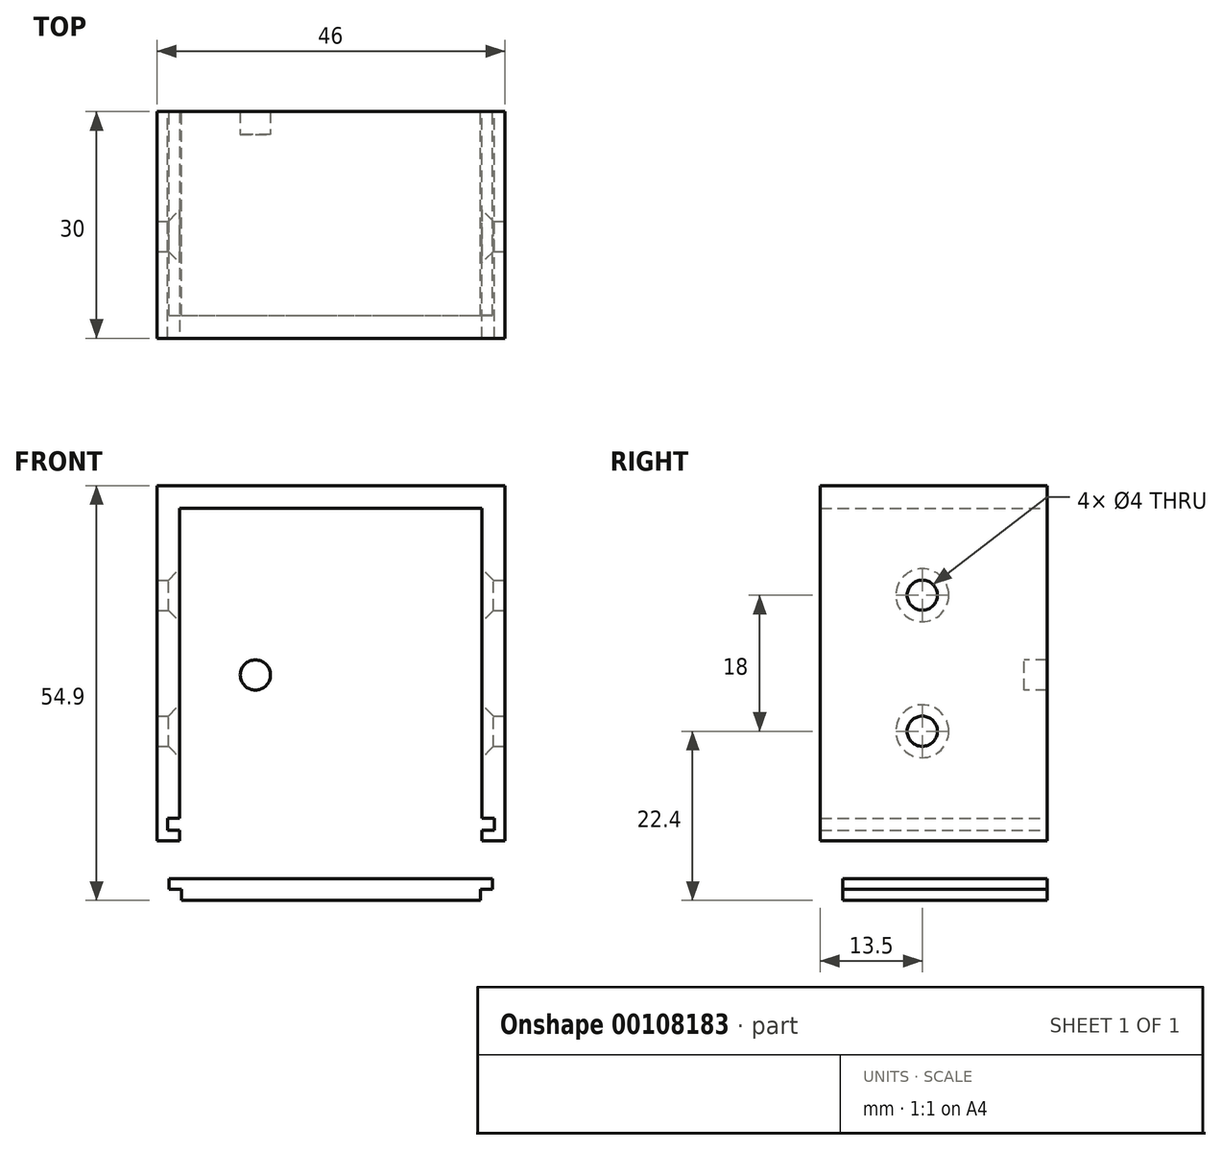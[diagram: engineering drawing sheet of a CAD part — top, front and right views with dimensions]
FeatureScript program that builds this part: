
annotation { "Feature Type Name" : "Feature", "Feature Type Description" : "" }
export const myFeature = defineFeature(function(context is Context, id is Id, definition is map)
    precondition{}
    {
        {
            var Q0;
            Q0=qCreatedBy(makeId("Front.planeOp"),FACE);
            var sketch = newSketch(context, id + "F0", { "sketchPlane" : qUnion([Q0])});
            skLineSegment(sketch, "E0", {"start": v(0, 44) * mm, "end": v(20, 44) * mm});
            skLineSegment(sketch, "E1", {"start": v(20, 44) * mm, "end": v(20, 3) * mm});
            skLineSegment(sketch, "E2", {"start": v(20, 3) * mm, "end": v(21.6, 3) * mm});
            skLineSegment(sketch, "E3", {"start": v(21.6, 3) * mm, "end": v(21.6, 1.4) * mm});
            skLineSegment(sketch, "E4", {"start": v(21.6, 1.4) * mm, "end": v(20, 1.4) * mm});
            skLineSegment(sketch, "E5", {"start": v(20, 1.4) * mm, "end": v(20, 0) * mm});
            skLineSegment(sketch, "E6", {"start": v(20, 0) * mm, "end": v(23, 0) * mm});
            skLineSegment(sketch, "E7", {"start": v(23, 0) * mm, "end": v(23, 47) * mm});
            skLineSegment(sketch, "E8", {"start": v(23, 47) * mm, "end": v(0, 47) * mm});
            skLineSegment(sketch, "E9.MirrorCS", {"start": v(-23, 47) * mm, "end": v(0, 47) * mm});
            skLineSegment(sketch, "E10.MirrorCS", {"start": v(-23, 0) * mm, "end": v(-23, 47) * mm});
            skLineSegment(sketch, "E11.MirrorCS", {"start": v(0, 44) * mm, "end": v(-20, 44) * mm});
            skLineSegment(sketch, "E12.MirrorCS", {"start": v(-20, 44) * mm, "end": v(-20, 3) * mm});
            skLineSegment(sketch, "E13.MirrorCS", {"start": v(-20, 3) * mm, "end": v(-21.6, 3) * mm});
            skLineSegment(sketch, "E14.MirrorCS", {"start": v(-21.6, 3) * mm, "end": v(-21.6, 1.4) * mm});
            skLineSegment(sketch, "E15.MirrorCS", {"start": v(-21.6, 1.4) * mm, "end": v(-20, 1.4) * mm});
            skLineSegment(sketch, "E16.MirrorCS", {"start": v(-20, 1.4) * mm, "end": v(-20, 0) * mm});
            skLineSegment(sketch, "E17.MirrorCS", {"start": v(-20, 0) * mm, "end": v(-23, 0) * mm});
            skSolve(sketch);
        }
        {
            var Q0;
            Q0=makeQuery(id+"F0.imprint","IMPRINT",FACE,{"disambiguationData":[TD([[makeQuery(id+"F0.imprint","IMPRINT",EDGE,{"derivedFrom":sQuery(id+"F0.wireOp",EDGE,"E0")}),1.0]])]});
            extrude(context, id + "F1", {"entities" : qUnion([Q0]), "depth" : 30 * mm});
        }
        {
            var Q0;
            Q0=qCreatedBy(makeId("Top.planeOp"),FACE);
            var sketch = newSketch(context, id + "F2", { "sketchPlane" : qUnion([Q0])});
            skLineSegment(sketch, "E18", {"start": v(-23, 0) * mm, "end": v(-23, -3) * mm});
            skLineSegment(sketch, "E19", {"start": v(-23, -3) * mm, "end": v(23, -3) * mm});
            skLineSegment(sketch, "E20", {"start": v(23, -3) * mm, "end": v(23, 0) * mm});
            skLineSegment(sketch, "E21", {"start": v(23, 0) * mm, "end": v(-23, 0) * mm});
            skSolve(sketch);
        }
        {
            var Q0;
            Q0=makeQuery(id+"F2.imprint","IMPRINT",FACE,{"disambiguationData":[TD([[makeQuery(id+"F2.imprint","IMPRINT",EDGE,{"derivedFrom":sQuery(id+"F2.wireOp",EDGE,"E18")}),1.0]])]});
            extrude(context, id + "F3", {"entities" : qUnion([Q0]), "operationType" : NewBodyOperationType.ADD, "depth" : 47 * mm});
        }
        {
            var Q0;
            Q0=makeQuery(id+"F3.opExtrude","SWEPT_FACE",FACE,{"disambiguationData":[OSD([sQuery(id+"F2.wireOp",EDGE,"E19")])]});
            var sketch = newSketch(context, id + "F4", { "sketchPlane" : qUnion([Q0])});
            skCircle(sketch, "E22", {"center": v(10, 21.94) * mm, "radius": 2 * mm});
            skCircle(sketch, "E23.MirrorC", {"center": v(-10, 21.94) * mm, "radius": 2 * mm});
            skSolve(sketch);
        }
        {
            var Q0;
            Q0=makeQuery(id+"F4.imprint","IMPRINT",FACE,{"disambiguationData":[TD([[makeQuery(id+"F4.imprint","IMPRINT",EDGE,{"derivedFrom":sQuery(id+"F4.wireOp",EDGE,"E23.MirrorC")}),-1.0]])]});
            var Q1;
            Q1=makeQuery(id+"F4.imprint","IMPRINT",FACE,{"disambiguationData":[TD([[makeQuery(id+"F4.imprint","IMPRINT",EDGE,{"derivedFrom":sQuery(id+"F4.wireOp",EDGE,"E22")}),1.0]])]});
            extrude(context, id + "F5", {"entities" : qUnion([Q0, Q1]), "operationType" : NewBodyOperationType.REMOVE, "endBound" : BoundingType.THROUGH_ALL, "oppositeDirection" : true, "depth" : 25 * mm});
        }
        {
            var Q0;
            Q0=qCreatedBy(makeId("Front.planeOp"),FACE);
            var sketch = newSketch(context, id + "F6", { "sketchPlane" : qUnion([Q0])});
            skLineSegment(sketch, "E24", {"start": v(0, -5) * mm, "end": v(21.4, -5) * mm});
            skLineSegment(sketch, "E25", {"start": v(21.4, -5) * mm, "end": v(21.4, -6.4) * mm});
            skLineSegment(sketch, "E26", {"start": v(21.4, -6.4) * mm, "end": v(19.8, -6.4) * mm});
            skLineSegment(sketch, "E27", {"start": v(19.8, -6.4) * mm, "end": v(19.8, -7.9) * mm});
            skLineSegment(sketch, "E28", {"start": v(19.8, -7.9) * mm, "end": v(0, -7.9) * mm});
            skLineSegment(sketch, "E29.MirrorCS", {"start": v(0, -5) * mm, "end": v(-21.4, -5) * mm});
            skLineSegment(sketch, "E30.MirrorCS", {"start": v(-19.8, -7.9) * mm, "end": v(0, -7.9) * mm});
            skLineSegment(sketch, "E31.MirrorCS", {"start": v(-19.8, -6.4) * mm, "end": v(-19.8, -7.9) * mm});
            skLineSegment(sketch, "E32.MirrorCS", {"start": v(-21.4, -6.4) * mm, "end": v(-19.8, -6.4) * mm});
            skLineSegment(sketch, "E33.MirrorCS", {"start": v(-21.4, -5) * mm, "end": v(-21.4, -6.4) * mm});
            skSolve(sketch);
        }
        {
            var Q0;
            Q0=makeQuery(id+"F6.imprint","IMPRINT",FACE,{"disambiguationData":[TD([[makeQuery(id+"F6.imprint","IMPRINT",EDGE,{"derivedFrom":sQuery(id+"F6.wireOp",EDGE,"E24")}),-1.0]])]});
            extrude(context, id + "F7", {"entities" : qUnion([Q0]), "depth" : 27 * mm});
        }
        {
            var Q0;
            Q0=makeQuery(id+"F1.opExtrude","SWEPT_FACE",FACE,{"disambiguationData":[OSD([sQuery(id+"F0.wireOp",EDGE,"E7")])]});
            var sketch = newSketch(context, id + "F8", { "sketchPlane" : qUnion([Q0])});
            skCircle(sketch, "E34", {"center": v(-16.5, 32.5) * mm, "radius": 2 * mm});
            skCircle(sketch, "E35", {"center": v(-16.5, 14.5) * mm, "radius": 2 * mm});
            skSolve(sketch);
        }
        {
            var Q0;
            Q0=makeQuery(id+"F8.imprint","IMPRINT",FACE,{"disambiguationData":[TD([[makeQuery(id+"F8.imprint","IMPRINT",EDGE,{"derivedFrom":sQuery(id+"F8.wireOp",EDGE,"E34")}),1.0]])]});
            var Q1;
            Q1=makeQuery(id+"F8.imprint","IMPRINT",FACE,{"disambiguationData":[TD([[makeQuery(id+"F8.imprint","IMPRINT",EDGE,{"derivedFrom":sQuery(id+"F8.wireOp",EDGE,"E35")}),1.0]])]});
            extrude(context, id + "F9", {"entities" : qUnion([Q0, Q1]), "operationType" : NewBodyOperationType.REMOVE, "oppositeDirection" : true, "depth" : 50 * mm});
        }
        {
            var Q0;
            Q0=makeQuery(id+"F9.boolean.opBoolean","INTERSECT",EDGE,{"derivedFrom":[makeQuery(id+"F1.opExtrude","SWEPT_FACE",FACE,{"disambiguationData":[OSD([sQuery(id+"F0.wireOp",EDGE,"E1")])]}),makeQuery(id+"F9.opExtrude","SWEPT_FACE",FACE,{"disambiguationData":[OSD([sQuery(id+"F8.wireOp",EDGE,"E34")])]})]});
            var Q1;
            Q1=makeQuery(id+"F9.boolean.opBoolean","INTERSECT",EDGE,{"derivedFrom":[makeQuery(id+"F1.opExtrude","SWEPT_FACE",FACE,{"disambiguationData":[OSD([sQuery(id+"F0.wireOp",EDGE,"E1")])]}),makeQuery(id+"F9.opExtrude","SWEPT_FACE",FACE,{"disambiguationData":[OSD([sQuery(id+"F8.wireOp",EDGE,"E35")])]})]});
            var Q2;
            Q2=makeQuery(id+"F9.boolean.opBoolean","INTERSECT",EDGE,{"derivedFrom":[makeQuery(id+"F1.opExtrude","SWEPT_FACE",FACE,{"disambiguationData":[OSD([sQuery(id+"F0.wireOp",EDGE,"E12.MirrorCS")])]}),makeQuery(id+"F9.opExtrude","SWEPT_FACE",FACE,{"disambiguationData":[OSD([sQuery(id+"F8.wireOp",EDGE,"E34")])]})]});
            var Q3;
            Q3=makeQuery(id+"F9.boolean.opBoolean","INTERSECT",EDGE,{"derivedFrom":[makeQuery(id+"F1.opExtrude","SWEPT_FACE",FACE,{"disambiguationData":[OSD([sQuery(id+"F0.wireOp",EDGE,"E12.MirrorCS")])]}),makeQuery(id+"F9.opExtrude","SWEPT_FACE",FACE,{"disambiguationData":[OSD([sQuery(id+"F8.wireOp",EDGE,"E35")])]})]});
            var Q4;
            Q4=makeQuery(id+"F5.boolean.opBoolean","COPY",EDGE,{"derivedFrom":makeQuery(id+"F5.opExtrude","CAP_EDGE",EDGE,{"disambiguationData":[OSD([sQuery(id+"F4.wireOp",EDGE,"E23.MirrorC")])],"isStart":true})});
            var Q5;
            Q5=makeQuery(id+"F5.boolean.opBoolean","COPY",EDGE,{"derivedFrom":makeQuery(id+"F5.opExtrude","CAP_EDGE",EDGE,{"disambiguationData":[OSD([sQuery(id+"F4.wireOp",EDGE,"E22")])],"isStart":true})});
            chamfer(context, id + "F10", {"entities" : qUnion([Q0, Q1, Q2, Q3, Q4, Q5]), "width" : 1.5 * mm, "tangentPropagation" : true});
        }
    });
